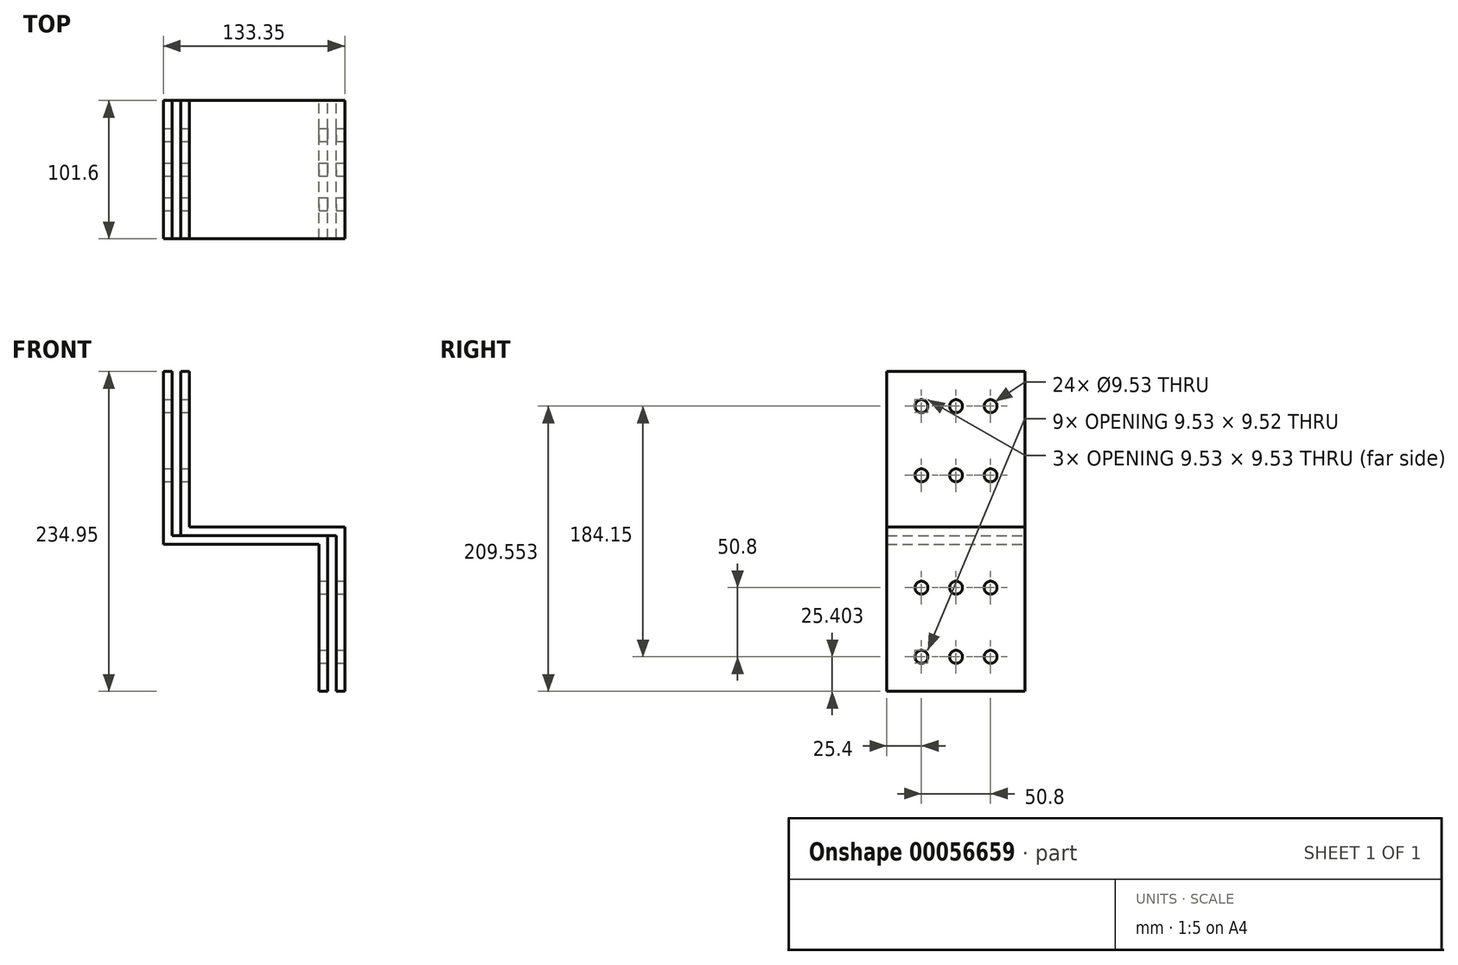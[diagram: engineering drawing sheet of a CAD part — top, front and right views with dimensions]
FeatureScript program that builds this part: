
annotation { "Feature Type Name" : "Feature", "Feature Type Description" : "" }
export const myFeature = defineFeature(function(context is Context, id is Id, definition is map)
    precondition{}
    {
        {
            var Q0;
            Q0=qCreatedBy(makeId("Front.planeOp"),FACE);
            var sketch = newSketch(context, id + "F0", { "sketchPlane" : qUnion([Q0])});
            skLineSegment(sketch, "E0", {"start": v(-5.98, -102.5) * mm, "end": v(-5.98, 5.44) * mm});
            skLineSegment(sketch, "E1", {"start": v(-5.98, 5.44) * mm, "end": v(-120.28, 5.44) * mm});
            skLineSegment(sketch, "E2", {"start": v(-120.28, 5.44) * mm, "end": v(-120.28, 132.44) * mm});
            skLineSegment(sketch, "E3", {"start": v(-113.93, 11.8) * mm, "end": v(0.37, 11.8) * mm});
            skLineSegment(sketch, "E4.trimOffspring", {"start": v(-113.93, 132.44) * mm, "end": v(-113.93, 11.8) * mm});
            skLineSegment(sketch, "E5", {"start": v(0.37, 11.8) * mm, "end": v(0.37, -102.5) * mm});
            skLineSegment(sketch, "E6", {"start": v(0.37, -102.5) * mm, "end": v(-5.98, -102.5) * mm});
            skLineSegment(sketch, "E7", {"start": v(-113.93, 132.44) * mm, "end": v(-120.28, 132.44) * mm});
            skSolve(sketch);
        }
        {
            var Q0;
            Q0 = qSketchRegion(id + "F0", true);
            extrude(context, id + "F1", {"entities" : qUnion([Q0]), "endBound" : BoundingType.SYMMETRIC, "depth" : 101.6 * mm});
        }
        {
            var Q0;
            Q0=qCreatedBy(makeId("Front.planeOp"),FACE);
            var sketch = newSketch(context, id + "F2", { "sketchPlane" : qUnion([Q0])});
            skLineSegment(sketch, "E8", {"start": v(6.72, -102.5) * mm, "end": v(6.72, 11.8) * mm});
            skLineSegment(sketch, "E9", {"start": v(6.72, 11.8) * mm, "end": v(-107.58, 11.8) * mm});
            skLineSegment(sketch, "E10", {"start": v(-107.58, 11.8) * mm, "end": v(-107.58, 132.44) * mm});
            skLineSegment(sketch, "E11", {"start": v(-101.23, 18.14) * mm, "end": v(13.07, 18.14) * mm});
            skLineSegment(sketch, "E12.trimOffspring", {"start": v(-101.23, 132.44) * mm, "end": v(-101.23, 18.14) * mm});
            skLineSegment(sketch, "E13", {"start": v(13.07, 18.14) * mm, "end": v(13.07, -102.5) * mm});
            skLineSegment(sketch, "E14", {"start": v(13.07, -102.5) * mm, "end": v(6.72, -102.5) * mm});
            skLineSegment(sketch, "E15", {"start": v(-101.23, 132.44) * mm, "end": v(-107.58, 132.44) * mm});
            skSolve(sketch);
        }
        {
            var Q0;
            Q0 = qSketchRegion(id + "F2", true);
            extrude(context, id + "F3", {"entities" : qUnion([Q0]), "endBound" : BoundingType.SYMMETRIC, "depth" : 101.6 * mm});
        }
        {
            var Q0;
            Q0=makeQuery(id+"F3.opExtrude","SWEPT_FACE",FACE,{"disambiguationData":[OSD([sQuery(id+"F2.wireOp",EDGE,"E13")])]});
            var sketch = newSketch(context, id + "F4", { "sketchPlane" : qUnion([Q0])});
            skCircle(sketch, "E16", {"center": v(-25.4, -77.1) * mm, "radius": 4.76 * mm});
            skCircle(sketch, "E17", {"center": v(-25.4, 107.04) * mm, "radius": 4.76 * mm});
            skCircle(sketch, "E18.0.1.0", {"center": v(-25.4, 56.24) * mm, "radius": 4.76 * mm});
            skCircle(sketch, "E18.1.0.0", {"center": v(0, 107.04) * mm, "radius": 4.76 * mm});
            skCircle(sketch, "E18.1.1.0", {"center": v(0, 56.24) * mm, "radius": 4.76 * mm});
            skCircle(sketch, "E18.2.0.0", {"center": v(25.4, 107.04) * mm, "radius": 4.76 * mm});
            skCircle(sketch, "E18.2.1.0", {"center": v(25.4, 56.24) * mm, "radius": 4.76 * mm});
            skLineSegment(sketch, "E18.direction1", {"start": v(-25.4, 107.04) * mm, "end": v(0, 107.04) * mm, "construction": true});
            skLineSegment(sketch, "E18.direction2", {"start": v(-25.4, 107.04) * mm, "end": v(-25.4, 56.24) * mm, "construction": true});
            skCircle(sketch, "E19.0.1.0", {"center": v(-25.4, -26.3) * mm, "radius": 4.76 * mm});
            skCircle(sketch, "E19.1.0.0", {"center": v(0, -77.1) * mm, "radius": 4.76 * mm});
            skCircle(sketch, "E19.1.1.0", {"center": v(0, -26.3) * mm, "radius": 4.76 * mm});
            skCircle(sketch, "E19.2.0.0", {"center": v(25.4, -77.1) * mm, "radius": 4.76 * mm});
            skCircle(sketch, "E19.2.1.0", {"center": v(25.4, -26.3) * mm, "radius": 4.76 * mm});
            skLineSegment(sketch, "E19.direction1", {"start": v(-25.4, -77.1) * mm, "end": v(0, -77.1) * mm, "construction": true});
            skLineSegment(sketch, "E19.direction2", {"start": v(-25.4, -77.1) * mm, "end": v(-25.4, -26.3) * mm, "construction": true});
            skSolve(sketch);
        }
        {
            var Q0;
            Q0 = qSketchRegion(id + "F4", true);
            extrude(context, id + "F5", {"entities" : qUnion([Q0]), "operationType" : NewBodyOperationType.REMOVE, "endBound" : BoundingType.THROUGH_ALL, "oppositeDirection" : true, "depth" : 25.4 * mm});
        }
    });
